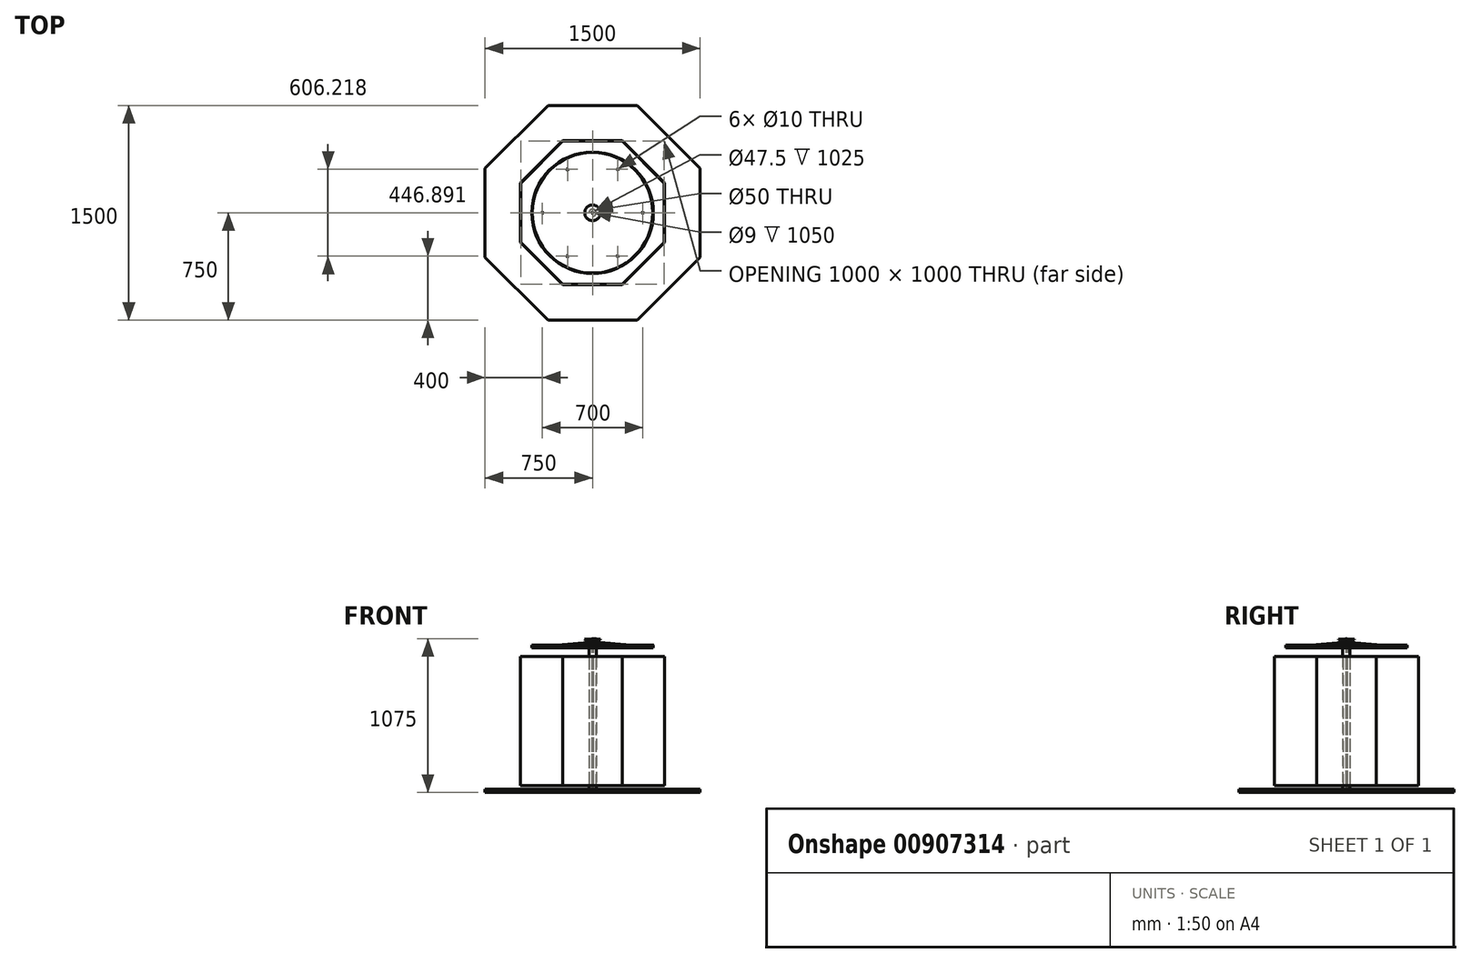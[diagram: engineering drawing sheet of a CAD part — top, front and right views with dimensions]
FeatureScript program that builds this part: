
annotation { "Feature Type Name" : "Feature", "Feature Type Description" : "" }
export const myFeature = defineFeature(function(context is Context, id is Id, definition is map)
    precondition{}
    {
        {
            var Q0;
            Q0=qCreatedBy(makeId("Top.planeOp"),FACE);
            var sketch = newSketch(context, id + "F0", { "sketchPlane" : qUnion([Q0])});
            skCircle(sketch, "E0.cCircle", {"center": v(0, 0) * mm, "radius": 500 * mm, "construction": true});
            skLineSegment(sketch, "E0.0", {"start": v(-207.1, 500) * mm, "end": v(207.1, 500) * mm});
            skLineSegment(sketch, "E0.1", {"start": v(207.1, 500) * mm, "end": v(500, 207.1) * mm});
            skLineSegment(sketch, "E0.2", {"start": v(500, 207.1) * mm, "end": v(500, -207.1) * mm});
            skLineSegment(sketch, "E0.3", {"start": v(500, -207.1) * mm, "end": v(207.1, -500) * mm});
            skLineSegment(sketch, "E0.4", {"start": v(207.1, -500) * mm, "end": v(-207.1, -500) * mm});
            skLineSegment(sketch, "E0.5", {"start": v(-207.1, -500) * mm, "end": v(-500, -207.1) * mm});
            skLineSegment(sketch, "E0.6", {"start": v(-500, -207.1) * mm, "end": v(-500, 207.1) * mm});
            skLineSegment(sketch, "E0.7", {"start": v(-500, 207.1) * mm, "end": v(-207.1, 500) * mm});
            skPoint(sketch, "E0.0.midPoint", {"position": v(0, 500) * mm});
            skCircle(sketch, "E1", {"center": v(0, 0) * mm, "radius": 5 * mm});
            skCircle(sketch, "E2", {"center": v(0, 0) * mm, "radius": 4.5 * mm});
            skCircle(sketch, "E3", {"center": v(0, 0) * mm, "radius": 25 * mm});
            skCircle(sketch, "E4", {"center": v(0, 0) * mm, "radius": 23.75 * mm});
            skLineSegment(sketch, "E5.0", {"start": v(208.35, 503) * mm, "end": v(503, 208.35) * mm});
            skLineSegment(sketch, "E5.1", {"start": v(-208.35, 503) * mm, "end": v(208.35, 503) * mm});
            skLineSegment(sketch, "E5.2", {"start": v(503, 208.35) * mm, "end": v(503, -208.35) * mm});
            skLineSegment(sketch, "E5.3", {"start": v(-503, 208.35) * mm, "end": v(-208.35, 503) * mm});
            skLineSegment(sketch, "E5.4", {"start": v(503, -208.35) * mm, "end": v(208.35, -503) * mm});
            skLineSegment(sketch, "E5.5", {"start": v(208.35, -503) * mm, "end": v(-208.35, -503) * mm});
            skLineSegment(sketch, "E5.6", {"start": v(-208.35, -503) * mm, "end": v(-503, -208.35) * mm});
            skLineSegment(sketch, "E5.7", {"start": v(-503, -208.35) * mm, "end": v(-503, 208.35) * mm});
            skSolve(sketch);
        }
        {
            var Q0;
            Q0=makeQuery(id+"F0.imprint","IMPRINT",FACE,{"disambiguationData":[TD([[makeQuery(id+"F0.imprint","IMPRINT",EDGE,{"derivedFrom":sQuery(id+"F0.wireOp",EDGE,"E3")}),1.0]])]});
            var Q1;
            Q1=makeQuery(id+"F0.imprint","IMPRINT",FACE,{"disambiguationData":[TD([[makeQuery(id+"F0.imprint","IMPRINT",EDGE,{"derivedFrom":sQuery(id+"F0.wireOp",EDGE,"E1")}),1.0]])]});
            extrude(context, id + "F1", {"entities" : qUnion([Q0, Q1]), "depth" : 1000 * mm, "offsetDistance" : 25 * mm});
        }
        {
            var Q0;
            Q0=makeQuery(id+"F1.opExtrude","CAP_FACE",FACE,{"disambiguationData":[OSD([sQuery(id+"F0.wireOp",EDGE,"E1"),sQuery(id+"F0.wireOp",EDGE,"E2")])],"isStart":false});
            extrude(context, id + "F2", {"entities" : qUnion([Q0]), "operationType" : NewBodyOperationType.ADD, "depth" : 25 * mm, "offsetDistance" : 25 * mm});
        }
        {
            var Q0;
            Q0=qCreatedBy(makeId("Front.planeOp"),FACE);
            var sketch = newSketch(context, id + "F3", { "sketchPlane" : qUnion([Q0])});
            skLineSegment(sketch, "E6.0", {"start": v(-25, 1000) * mm, "end": v(25, 1000) * mm});
            skLineSegment(sketch, "E7", {"start": v(-25, 1000) * mm, "end": v(-423.48, 965.14) * mm});
            skLineSegment(sketch, "E8", {"start": v(-423.48, 965.14) * mm, "end": v(-423.22, 962.15) * mm});
            skLineSegment(sketch, "E9", {"start": v(-423.22, 962.15) * mm, "end": v(-25, 996.99) * mm});
            skLineSegment(sketch, "E10", {"start": v(-25, 1000) * mm, "end": v(-25, 975.75) * mm});
            skLineSegment(sketch, "E11", {"start": v(0, 1000) * mm, "end": v(0, 865.1) * mm, "construction": true});
            skLineSegment(sketch, "E12.0", {"start": v(-5, 1025) * mm, "end": v(5, 1025) * mm});
            skLineSegment(sketch, "E13", {"start": v(-5, 1025) * mm, "end": v(-54.8, 1020.64) * mm});
            skLineSegment(sketch, "E14", {"start": v(-54.8, 1020.64) * mm, "end": v(-54.55, 1017.65) * mm});
            skLineSegment(sketch, "E15", {"start": v(-54.55, 1017.65) * mm, "end": v(-5, 1021.99) * mm});
            skLineSegment(sketch, "E16", {"start": v(-5, 1025) * mm, "end": v(-5, 1021.99) * mm});
            skLineSegment(sketch, "E17", {"start": v(-423.48, 965.14) * mm, "end": v(-424.79, 980.08) * mm});
            skLineSegment(sketch, "E18", {"start": v(-424.79, 980.08) * mm, "end": v(-421.8, 980.34) * mm});
            skLineSegment(sketch, "E19", {"start": v(-421.8, 980.34) * mm, "end": v(-420.47, 965.14) * mm});
            skSolve(sketch);
        }
        {
            var Q0;
            {var subQ0=sQuery(id+"F3.wireOp",EDGE,"E7");Q0=makeQuery(id+"F3.imprint","IMPRINT",FACE,{"disambiguationData":[TD([[makeQuery(id+"F3.imprint","IMPRINT",EDGE,{"derivedFrom":subQ0}),1.0]])]});}
            var Q1;
            {var subQ0=sQuery(id+"F3.wireOp",EDGE,"E17");Q1=makeQuery(id+"F3.imprint","IMPRINT",FACE,{"disambiguationData":[TD([[makeQuery(id+"F3.imprint","IMPRINT",EDGE,{"derivedFrom":subQ0}),-1.0]])]});}
            var Q2;
            Q2=sQuery(id+"F3.wireOp",EDGE,"E11");
            revolve(context, id + "F4", {"operationType" : NewBodyOperationType.ADD, "surfaceOperationType" : NewSurfaceOperationType.NEW, "entities" : qUnion([Q0, Q1]), "axis" : qUnion([Q2]), "revolveType" : RevolveType.FULL});
        }
        {
            var Q0;
            Q0=makeQuery(id+"F3.imprint","IMPRINT",FACE,{"disambiguationData":[TD([[makeQuery(id+"F3.imprint","IMPRINT",EDGE,{"derivedFrom":sQuery(id+"F3.wireOp",EDGE,"E13")}),1.0]])]});
            var Q1;
            Q1=sQuery(id+"F3.wireOp",EDGE,"E11");
            revolve(context, id + "F5", {"operationType" : NewBodyOperationType.ADD, "surfaceOperationType" : NewSurfaceOperationType.NEW, "entities" : qUnion([Q0]), "axis" : qUnion([Q1]), "revolveType" : RevolveType.FULL});
        }
        {
            var Q0;
            Q0=makeQuery(id+"F2.opExtrude","CAP_FACE",FACE,{"disambiguationData":[OSD([sQuery(id+"F0.wireOp",EDGE,"E1"),sQuery(id+"F0.wireOp",EDGE,"E2")])],"isStart":false});
            var sketch = newSketch(context, id + "F6", { "sketchPlane" : qUnion([Q0])});
            skLineSegment(sketch, "E20.0", {"start": v(-423.22, 0) * mm, "end": v(-25, 0) * mm, "construction": true});
            skCircle(sketch, "E21", {"center": v(-350, 0) * mm, "radius": 5 * mm});
            skCircle(sketch, "E22.1.0", {"center": v(-175, -303.1) * mm, "radius": 5 * mm});
            skCircle(sketch, "E22.2.0", {"center": v(175, -303.1) * mm, "radius": 5 * mm});
            skCircle(sketch, "E22.3.0", {"center": v(350, 0) * mm, "radius": 5 * mm});
            skCircle(sketch, "E22.4.0", {"center": v(175, 303.1) * mm, "radius": 5 * mm});
            skCircle(sketch, "E22.5.0", {"center": v(-175, 303.1) * mm, "radius": 5 * mm});
            skPoint(sketch, "E22.center", {"position": v(0, 0) * mm});
            skSolve(sketch);
        }
        {
            var Q0;
            Q0=makeQuery(id+"F6.imprint","IMPRINT",FACE,{"disambiguationData":[TD([[makeQuery(id+"F6.imprint","IMPRINT",EDGE,{"derivedFrom":sQuery(id+"F6.wireOp",EDGE,"E21")}),1.0]])]});
            var Q1;
            Q1=makeQuery(id+"F6.imprint","IMPRINT",FACE,{"disambiguationData":[TD([[makeQuery(id+"F6.imprint","IMPRINT",EDGE,{"derivedFrom":sQuery(id+"F6.wireOp",EDGE,"E22.5.0")}),1.0]])]});
            var Q2;
            Q2=makeQuery(id+"F6.imprint","IMPRINT",FACE,{"disambiguationData":[TD([[makeQuery(id+"F6.imprint","IMPRINT",EDGE,{"derivedFrom":sQuery(id+"F6.wireOp",EDGE,"E22.4.0")}),1.0]])]});
            var Q3;
            Q3=makeQuery(id+"F6.imprint","IMPRINT",FACE,{"disambiguationData":[TD([[makeQuery(id+"F6.imprint","IMPRINT",EDGE,{"derivedFrom":sQuery(id+"F6.wireOp",EDGE,"E22.3.0")}),1.0]])]});
            var Q4;
            Q4=makeQuery(id+"F6.imprint","IMPRINT",FACE,{"disambiguationData":[TD([[makeQuery(id+"F6.imprint","IMPRINT",EDGE,{"derivedFrom":sQuery(id+"F6.wireOp",EDGE,"E22.2.0")}),1.0]])]});
            var Q5;
            Q5=makeQuery(id+"F6.imprint","IMPRINT",FACE,{"disambiguationData":[TD([[makeQuery(id+"F6.imprint","IMPRINT",EDGE,{"derivedFrom":sQuery(id+"F6.wireOp",EDGE,"E22.1.0")}),1.0]])]});
            extrude(context, id + "F7", {"entities" : qUnion([Q0, Q1, Q2, Q3, Q4, Q5]), "operationType" : NewBodyOperationType.REMOVE, "endBound" : BoundingType.THROUGH_ALL, "oppositeDirection" : true, "depth" : 25 * mm, "offsetDistance" : 25 * mm});
        }
        {
            var Q0;
            Q0=makeQuery(id+"F0.imprint","IMPRINT",FACE,{"disambiguationData":[TD([[makeQuery(id+"F0.imprint","IMPRINT",EDGE,{"derivedFrom":sQuery(id+"F0.wireOp",EDGE,"E0.0")}),1.0]])]});
            extrude(context, id + "F8", {"entities" : qUnion([Q0]), "depth" : 900 * mm, "offsetDistance" : 25 * mm});
        }
        {
            var Q0;
            Q0=makeQuery(id+"F0.imprint","IMPRINT",FACE,{"disambiguationData":[TD([[makeQuery(id+"F0.imprint","IMPRINT",EDGE,{"derivedFrom":sQuery(id+"F0.wireOp",EDGE,"E3")}),1.0]])]});
            var Q1;
            Q1=makeQuery(id+"F0.imprint","IMPRINT",FACE,{"disambiguationData":[TD([[makeQuery(id+"F0.imprint","IMPRINT",EDGE,{"derivedFrom":sQuery(id+"F0.wireOp",EDGE,"E1")}),1.0]])]});
            extrude(context, id + "F9", {"entities" : qUnion([Q0, Q1]), "operationType" : NewBodyOperationType.ADD, "oppositeDirection" : true, "depth" : 25 * mm, "offsetDistance" : 25 * mm});
        }
        {
            var Q0;
            Q0=makeQuery(id+"F9.opExtrude","CAP_FACE",FACE,{"disambiguationData":[OSD([sQuery(id+"F0.wireOp",EDGE,"E3"),sQuery(id+"F0.wireOp",EDGE,"E4")])],"isStart":false});
            var sketch = newSketch(context, id + "F10", { "sketchPlane" : qUnion([Q0])});
            skCircle(sketch, "E23.0", {"center": v(0, 0) * mm, "radius": 23.75 * mm});
            skCircle(sketch, "E24.cCircle", {"center": v(0, 0) * mm, "radius": 750 * mm, "construction": true});
            skLineSegment(sketch, "E24.0", {"start": v(750, -310.66) * mm, "end": v(310.66, -750) * mm});
            skLineSegment(sketch, "E24.1", {"start": v(310.66, -750) * mm, "end": v(-310.66, -750) * mm});
            skLineSegment(sketch, "E24.2", {"start": v(-310.66, -750) * mm, "end": v(-750, -310.66) * mm});
            skLineSegment(sketch, "E24.3", {"start": v(-750, -310.66) * mm, "end": v(-750, 310.66) * mm});
            skLineSegment(sketch, "E24.4", {"start": v(-750, 310.66) * mm, "end": v(-310.66, 750) * mm});
            skLineSegment(sketch, "E24.5", {"start": v(-310.66, 750) * mm, "end": v(310.66, 750) * mm});
            skLineSegment(sketch, "E24.6", {"start": v(310.66, 750) * mm, "end": v(750, 310.66) * mm});
            skLineSegment(sketch, "E24.7", {"start": v(750, 310.66) * mm, "end": v(750, -310.66) * mm});
            skPoint(sketch, "E24.0.midPoint", {"position": v(530.33, -530.33) * mm});
            skSolve(sketch);
        }
        {
            var Q0;
            Q0=makeQuery(id+"F10.imprint","IMPRINT",FACE,{"disambiguationData":[TD([[makeQuery(id+"F10.imprint","IMPRINT",EDGE,{"derivedFrom":sQuery(id+"F10.wireOp",EDGE,"E24.0")}),-1.0]])]});
            extrude(context, id + "F11", {"entities" : qUnion([Q0]), "depth" : 25 * mm, "offsetDistance" : 25 * mm});
        }
    });
